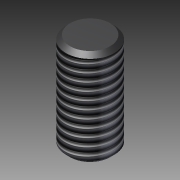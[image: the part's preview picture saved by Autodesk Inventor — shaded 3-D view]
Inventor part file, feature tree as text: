
AUTODESK INVENTOR PART (.ipt)
format: ipt  version: 2011 (Build 150229000, 229)  size: 109,568 bytes
history: native  units: mm (DEFAULTED — no unit token found)
features: extrude x2, sketch x2, chamfer x1, thread x1
ambient origin geometry x8: Origin, YZ Plane, XZ Plane, XY Plane, X Axis, Y Axis, Z Axis, Center Point
bodies: Solid1 (feature_tree)
feature tree (6):
  extrude  "Extrusion1"  Depth=12.0mm TaperAngle=0.0deg
  chamfer  "Chamfer1"  Distance=0.5mm
  extrude  "Extrusion2"  Depth=1.5mm
  thread  "Thread1"  [1 undecoded]
  sketch  "Sketch1"  dims[d0=6.0mm d1=12.0mm d2=0.0mm d3=0.5mm d4=0.5mm]
  sketch  "Sketch2"  dims[d5=3.232051mm d10=1.5mm d11=120.0deg d13=120.0deg d16=3.0mm d17=4.0mm d18=0.0mm d19=10.0mm d20=0.0mm d21=45.0deg]
note: 1 required parameter value undecoded (feature->parameter linkage not recoverable at this tier; creation-order binding heuristic only, values carry confidence <= 0.55)
